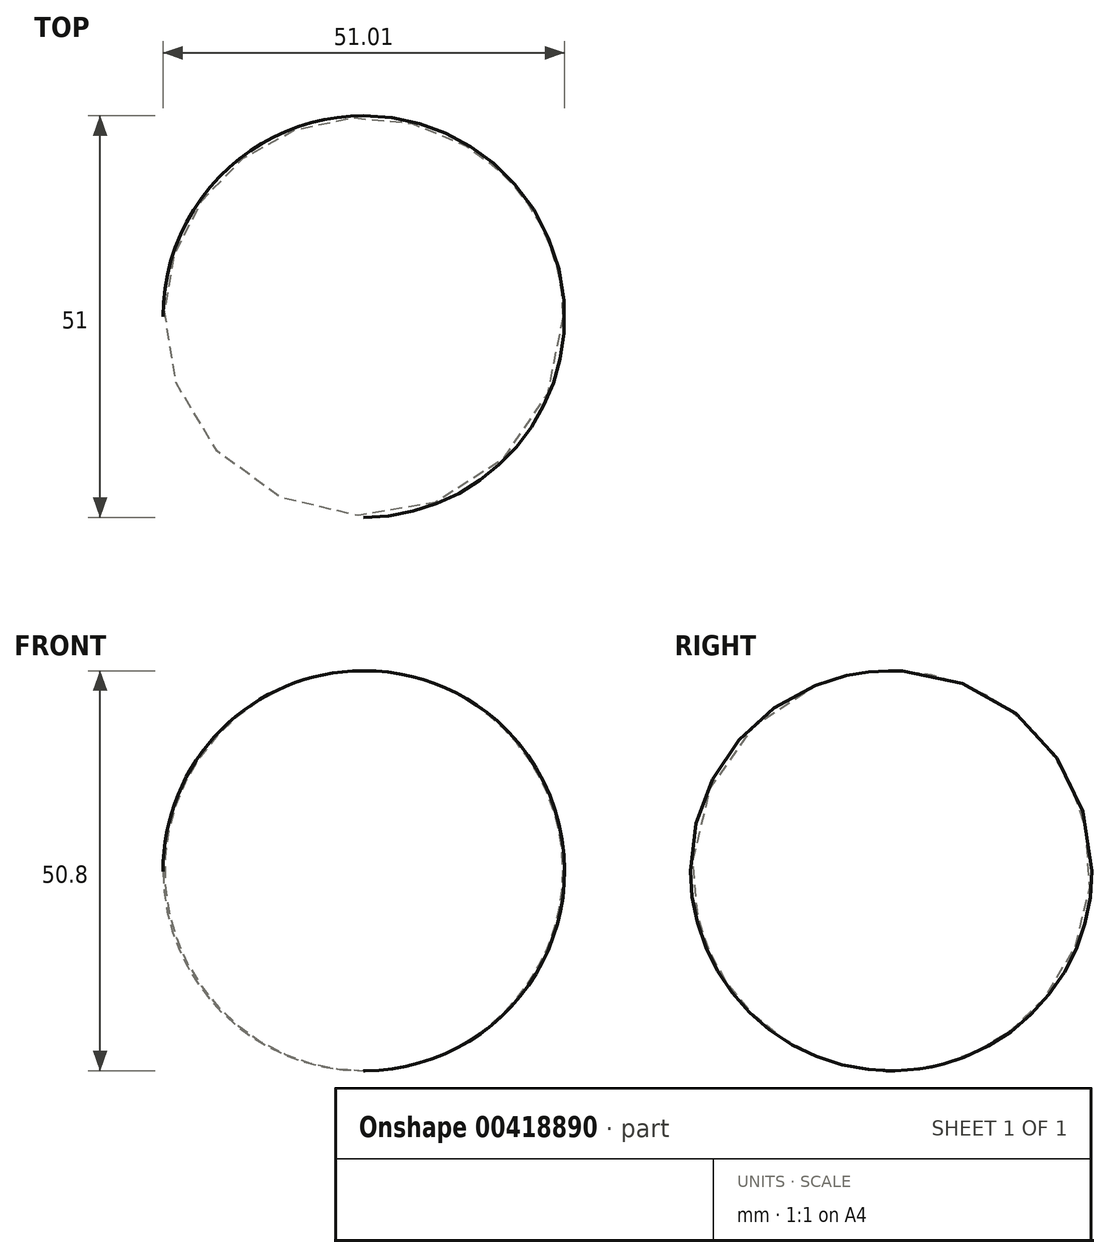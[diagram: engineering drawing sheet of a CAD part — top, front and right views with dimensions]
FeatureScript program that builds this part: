
annotation { "Feature Type Name" : "Feature", "Feature Type Description" : "" }
export const myFeature = defineFeature(function(context is Context, id is Id, definition is map)
    precondition{}
    {
        {
            var Q0;
            Q0=qCreatedBy(makeId("Front.planeOp"),FACE);
            var sketch = newSketch(context, id + "F0", { "sketchPlane" : qUnion([Q0])});
            skLineSegment(sketch, "E0", {"start": v(0.02, 25.4) * mm, "end": v(0.02, 25.4) * mm});
            skLineSegment(sketch, "E1", {"start": v(0.2, -25.4) * mm, "end": v(0.2, -25.4) * mm});
            skArc(sketch, "E2", {"start": v(0.02, 25.4) * mm, "mid": v(-25.4, -0.09) * mm, "end": v(0.2, -25.4) * mm});
            skLineSegment(sketch, "E3", {"start": v(0.02, 25.4) * mm, "end": v(0.2, -25.4) * mm});
            skSolve(sketch);
        }
        {
            var Q0;
            Q0=sQuery(id+"F0.wireOp",EDGE,"E2");
            var Q1;
            Q1=sQuery(id+"F0.wireOp",EDGE,"E3");
            revolve(context, id + "F1", {"bodyType" : ToolBodyType.SURFACE, "surfaceEntities" : qUnion([Q0]), "axis" : qUnion([Q1]), "revolveType" : RevolveType.FULL});
        }
    });
